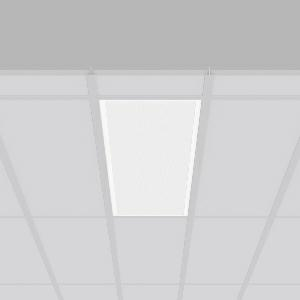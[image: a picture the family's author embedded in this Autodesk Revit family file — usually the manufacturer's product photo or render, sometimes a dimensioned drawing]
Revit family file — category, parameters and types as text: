
# Revit family: sidelite_eco_672369_002_1_7f79
name_source: partatom
category: Lighting Fixtures
units: mm (PartAtom-declared; Revit-internal decimal feet)

## family parameters
Cut with Voids When Loaded = No
Host = Face
Light Source = No
Part Type = Normal
Room Calculation Point = No
Round Connector Dimension = Use Diameter
Shared = No

## types (1)
- SIDELITE ECO (1 x LED Modul 840, 3450 lm, 4000)
    Apparent Load = 29 VA
    CIE Flux Codes = 59 87 97 100 100
    Color Rendering = 80
    Color Temperature = 4000
    Default Elevation = 1800 mm
    Description = Series: SIDELITE ECO
Highly economical recessed luminaire with progressive LED technology. For escape route illumination. Frame made of aluminium, powder-coated. Diffuser plastic microprismatic. Lightguide and diffuser made of non-yellowing plastic (PMMA). Lateral light emission (RZB SIDELITE technology) for homogeneous light distribution. External driver. Self-contained system with automatic self-test. External driver with simple plug-in locking system. Extended connection cable (1.90 m). 
Colour: white
Length: 1195 mm
Width: 295 mm
Cut-out length: 1170 mm
Cut-out width: 270 mm
Recess height: 160 mm
Luminaire: recess height: 40 mm
Weight: 4.41 kg
Operating mode: maintained power mode
Duration time: 8 h
Lamp: LED
Socket: without socket
Colour temperature: 4000K
Colour rendering index (CRI): 80
System power: 29 W
Rated luminous flux: 3450 lm
Luminous flux, emergency: 240 lm
System power, emergency: -
Control gear: Regulated power supply
Protection class: I
Type of protection: IP 40
    Height = 0 mm  [stored 0 ft]
    Lamp = 1 x LED Modul 840
    Lamp Light Flux = 3450 lm
    Lamp count = 1
    Length = 1195 mm
    Lifetime = 50000 h
    Luminous efficacy = 119 lm/W
    Manufacturer = RZB
    ModVariant = No
    Model = 672369.002.1
    Mounting Place = Ceiling
    Mounting Type = Recessed
    Number of Poles = 1
    OnlyDefault = Yes
    Power Factor = 1
    Product Name = SIDELITE ECO
    Product group = Recessed modular luminaires
    ProductGroupID = 406
    Protection Class = Protection class I
    Protection Degree = IP 40
    RLX_Detail_Level = 1
    RLX_Emergency_Light_Flux = 240 lm
    RLX_Emergency_Type = 3
    RLX_Emergency_Type_DB = Yes
    RlxData = <blob elided: 34605 chars, md5=b79eb359>
    Socket = socket
    Standby Power = 0 W
    System Light Flux = 3450 lm
    System Power = 29 W
    Type Comments = Product without accessories
    Type Image = 312366.002.jpg
    URL = http://relux.com
    VarID = ---
    Voltage = 230 V
    Voltage Range = 220-240 V
    Weight = 0.00 kg
    Width = 295 mm

note: [stored X ft] marks values corroborated as IEEE doubles in the binary element streams (Revit-internal decimal feet)

## geometry (parser evidence)
native form markers: Blend x4, Sweep x12
no freeform markers — native parametric forms only
